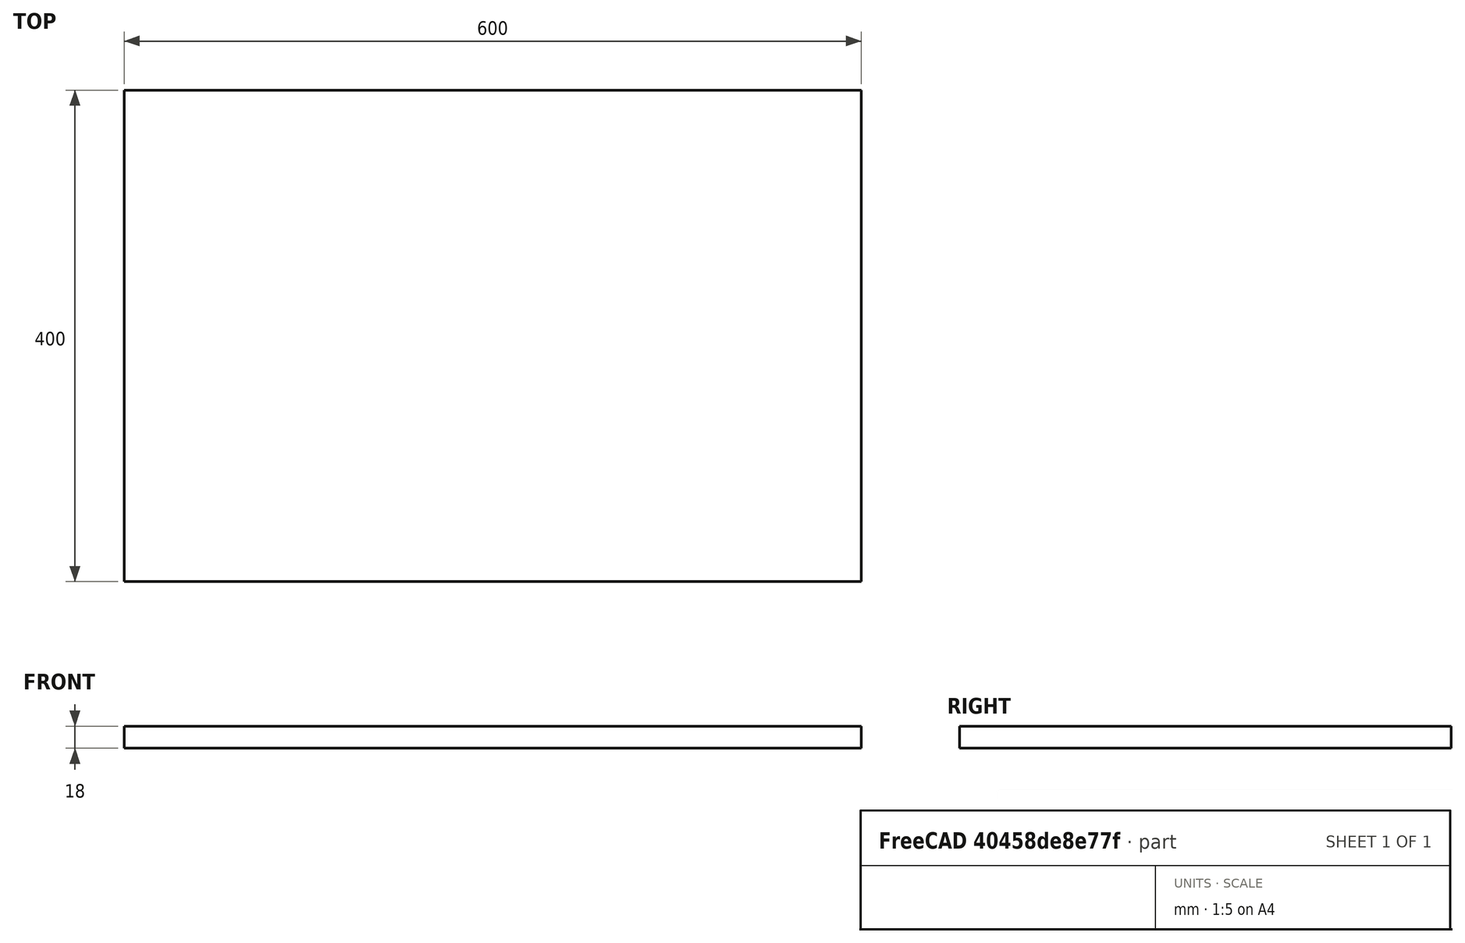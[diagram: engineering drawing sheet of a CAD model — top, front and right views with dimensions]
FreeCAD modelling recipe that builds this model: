
FCSTD DOCUMENT  (FreeCAD 0.18R4 (GitTag))
Label: bottom
License: All rights reserved
LicenseURL: http://en.wikipedia.org/wiki/All_rights_reserved
objects: Sketcher::SketchObject×1, PartDesign::Pad×1, PartDesign::Body×1
note: 4 computed .brp shape members not serialized (recipe doc carries the construction recipe); baked Part::Feature solids carry a one-line shape summary decoded from their .brp

FEATURE [Sketcher::SketchObject] Sketch
  MapMode = 5
  Support = -> [XY_Plane]
  sketch-geometry (4):
    g0: LineSegment StartX=0 StartY=0 StartZ=0 EndX=-600 EndY=0 EndZ=0
    g1: LineSegment StartX=-600 StartY=0 StartZ=0 EndX=-600 EndY=400 EndZ=0
    g2: LineSegment StartX=-600 StartY=400 StartZ=0 EndX=0 EndY=400 EndZ=0
    g3: LineSegment StartX=0 StartY=400 StartZ=0 EndX=0 EndY=0 EndZ=0
  constraints (11):
    c: Coincident(g0,g1)
    c: Coincident(g1,g2)
    c: Coincident(g2,g3)
    c: Coincident(g3,g0)
    c: Horizontal(g0)
    c: Horizontal(g2)
    c: Vertical(g1)
    c: Vertical(g3)
    c: Coincident(g0,g-1)
    c: DistanceY(g3,g3) = 400
    c: DistanceX(g0,g0) = 600
FEATURE [PartDesign::Pad] Pad
  Length = 18
  Length2 = 100
  Profile = -> Sketch
  Type = 0
FEATURE [PartDesign::Body] Body
  Group = -> [Sketch,Pad]
  Origin = -> Origin
  Tip = -> Pad
